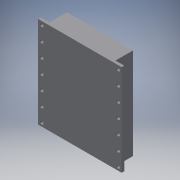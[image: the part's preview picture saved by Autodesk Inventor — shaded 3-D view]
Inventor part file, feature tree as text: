
AUTODESK INVENTOR PART (.ipt)
format: ipt  version: 2016 (Build 200138000, 138)  size: 124,416 bytes
history: native  units: mm
features: reference x14, sketch x3, extrude x2, hole x1
ambient origin geometry x8: Origin, YZ Plane, XZ Plane, XY Plane, X Axis, Y Axis, Z Axis, Center Point
bodies: Solid1 (feature_tree)
feature tree (20):
  extrude  "Extrusion1"  Depth=104.0mm
  extrude  "Extrusion2"  Depth=75.0mm
  hole  "Hole2"  [1 undecoded]
  sketch  "Sketch1"  dims[d0=95.0mm d1=104.0mm]
  sketch  "Sketch2"  dims[d2=3.0mm d3=0.0mm d4=75.0mm]
  sketch  "Sketch3"  dims[d5=104.0mm d6=20.0mm d7=0.0mm d8=4.0mm d9=4.0mm d10=4.0mm d11=4.0mm d19=4.0mm d20=6.0mm d21=4.0mm d22=2.0mm d23=90.0deg d24=8.0mm d25=20.594885mm]
  reference  "Reference1"
  reference  "Reference2"
  reference  "Reference3"
  reference  "Reference4"
  reference  "Reference5"
  reference  "Reference6"
  reference  "Reference7"
  reference  "Reference8"
  reference  "Reference9"
  reference  "Reference10"
  reference  "Reference11"
  reference  "Reference12"
  reference  "Reference13"
  reference  "Reference14"
note: 1 required parameter value undecoded (feature->parameter linkage not recoverable at this tier; creation-order binding heuristic only, values carry confidence <= 0.55)
